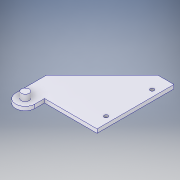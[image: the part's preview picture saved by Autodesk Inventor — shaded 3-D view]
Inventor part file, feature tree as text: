
AUTODESK INVENTOR PART (.ipt)
format: ipt  version: 2017 (Build 210142000, 142)  size: 120,832 bytes
history: native  units: in
note: dims shown in document units (in); Inventor stores cm internally (conversion verified against a paired STEP export)
features: extrude x2, sketch x2
ambient origin geometry x8: Origin, YZ Plane, XZ Plane, XY Plane, X Axis, Y Axis, Z Axis, Center Point
bodies: Solid1 (feature_tree)
feature tree (4):
  extrude  "Extrusion1"  TaperAngle=90.0deg  [1 undecoded]
  extrude  "Extrusion2"  Depth=1.6142in
  sketch  "Sketch3"  dims[d6=2.3622in d7=90.0deg]
  sketch  "Sketch4"  dims[d8=0.4929in d9=1.6142in d10=0.2953in d11=0.5906in d12=0.2362in d13=0.9456in d14=0.1181in d15=0.0in d16=0.315in d17=0.0in d18=0.1969in d19=0.4724in d20=0.4724in d21=0.1181in d22=0.1181in]
note: 1 required parameter value undecoded (feature->parameter linkage not recoverable at this tier; creation-order binding heuristic only, values carry confidence <= 0.55)
